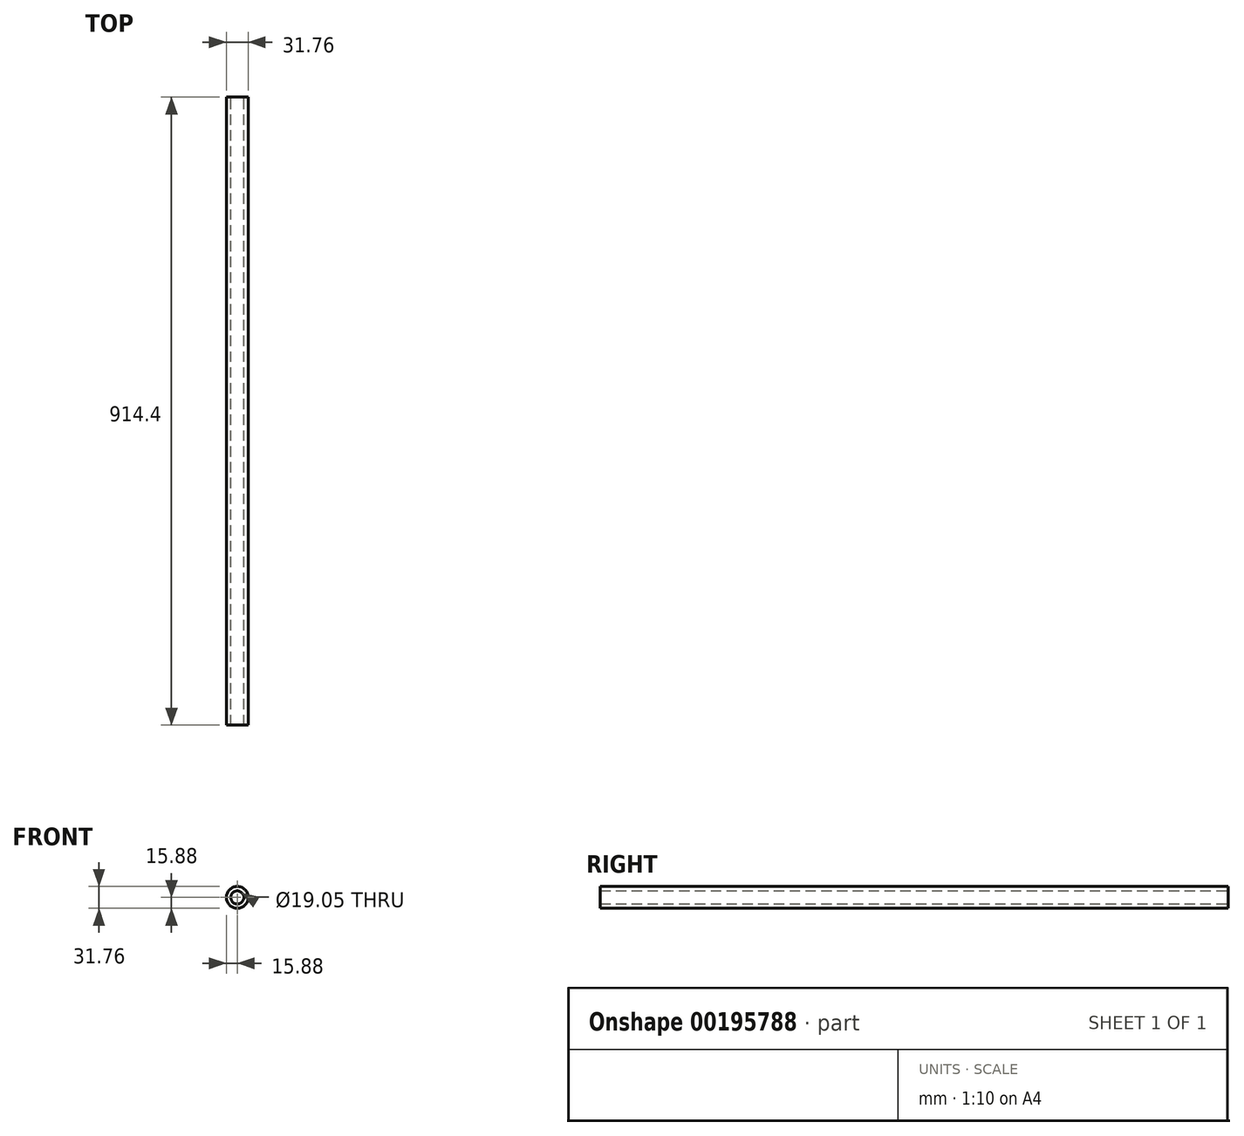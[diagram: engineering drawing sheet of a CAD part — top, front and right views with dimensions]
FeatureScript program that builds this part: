
annotation { "Feature Type Name" : "Feature", "Feature Type Description" : "" }
export const myFeature = defineFeature(function(context is Context, id is Id, definition is map)
    precondition{}
    {
        {
            var Q0;
            Q0=qCreatedBy(makeId("Front.planeOp"),FACE);
            var sketch = newSketch(context, id + "F0", { "sketchPlane" : qUnion([Q0])});
            skCircle(sketch, "E0", {"center": v(0, 0) * mm, "radius": 15.88 * mm});
            skCircle(sketch, "E1", {"center": v(0, 0) * mm, "radius": 9.53 * mm});
            skSolve(sketch);
        }
        {
            var Q0;
            Q0 = qSketchRegion(id + "F0", true);
            extrude(context, id + "F1", {"entities" : qUnion([Q0]), "depth" : 914.4 * mm});
        }
    });
